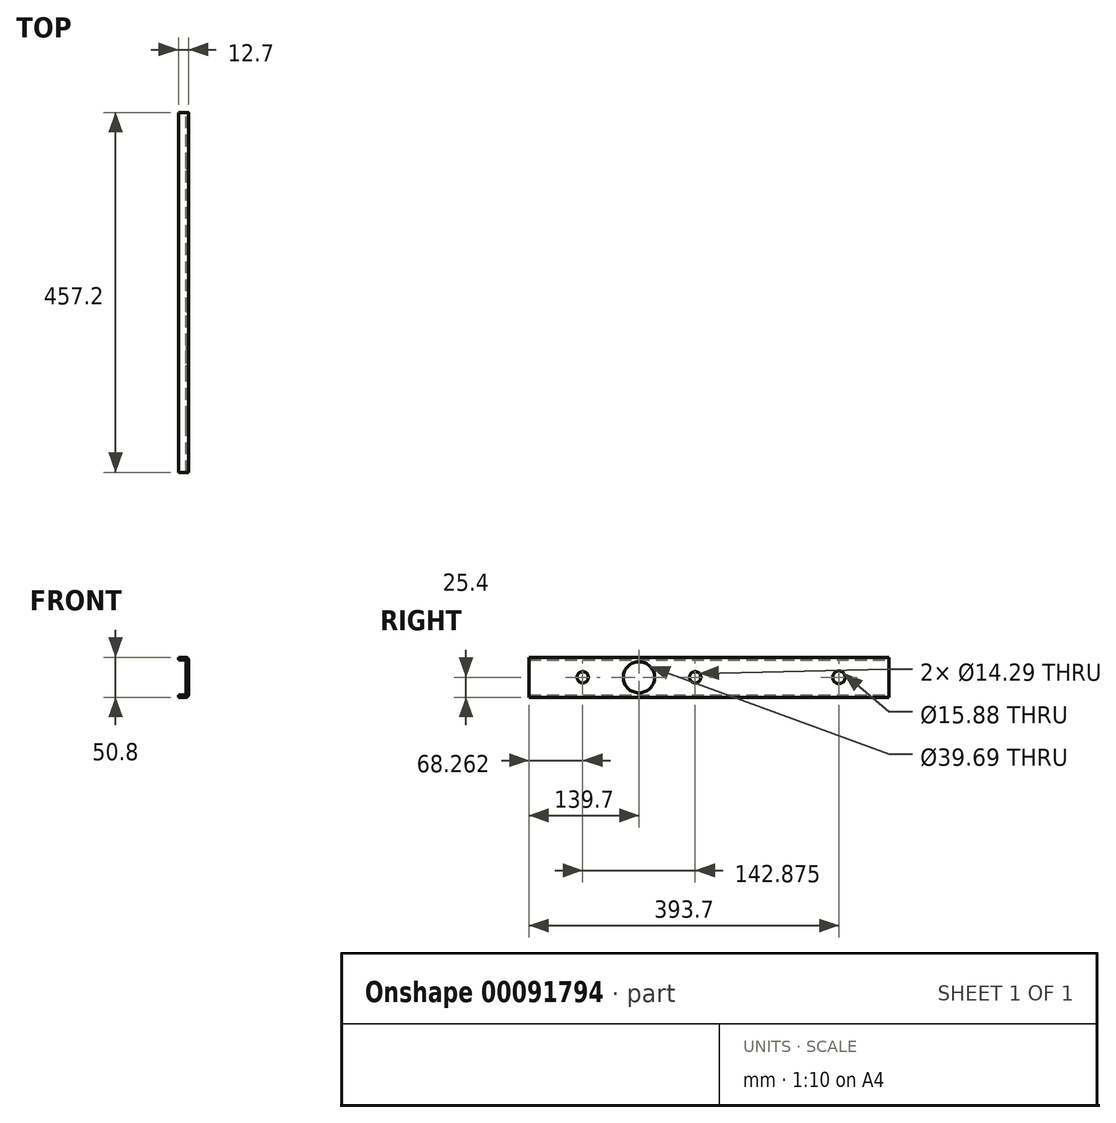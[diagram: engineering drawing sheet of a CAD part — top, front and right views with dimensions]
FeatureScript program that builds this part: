
annotation { "Feature Type Name" : "Feature", "Feature Type Description" : "" }
export const myFeature = defineFeature(function(context is Context, id is Id, definition is map)
    precondition{}
    {
        {
            var Q0;
            Q0=qCreatedBy(makeId("Front.planeOp"),FACE);
            var sketch = newSketch(context, id + "F0", { "sketchPlane" : qUnion([Q0])});
            skLineSegment(sketch, "E0", {"start": v(0, 0) * mm, "end": v(12.7, 0) * mm});
            skLineSegment(sketch, "E1", {"start": v(12.7, 0) * mm, "end": v(12.7, 50.8) * mm});
            skLineSegment(sketch, "E2", {"start": v(12.7, 50.8) * mm, "end": v(0, 50.8) * mm});
            skLineSegment(sketch, "E3", {"start": v(0, 50.8) * mm, "end": v(0, 47.63) * mm});
            skLineSegment(sketch, "E4", {"start": v(0, 47.63) * mm, "end": v(9.53, 47.63) * mm});
            skLineSegment(sketch, "E5", {"start": v(9.53, 47.63) * mm, "end": v(9.53, 3.18) * mm});
            skLineSegment(sketch, "E6", {"start": v(9.53, 3.18) * mm, "end": v(0, 3.18) * mm});
            skLineSegment(sketch, "E7", {"start": v(0, 3.18) * mm, "end": v(0, 0) * mm});
            skSolve(sketch);
        }
        {
            var Q0;
            Q0 = qSketchRegion(id + "F0", true);
            extrude(context, id + "F1", {"entities" : qUnion([Q0]), "depth" : 457.2 * mm});
        }
        {
            var Q0;
            Q0=makeQuery(id+"F1.opExtrude","SWEPT_EDGE",EDGE,{"disambiguationData":[OSD([sQuery(id+"F0.wireOp",EDGE,"E5"),sQuery(id+"F0.wireOp",EDGE,"E6")])]});
            var Q1;
            Q1=makeQuery(id+"F1.opExtrude","SWEPT_EDGE",EDGE,{"disambiguationData":[OSD([sQuery(id+"F0.wireOp",EDGE,"E4"),sQuery(id+"F0.wireOp",EDGE,"E5")])]});
            fillet(context, id + "F2", {"entities" : qUnion([Q0, Q1]), "radius" : 1.59 * mm, "tangentPropagation" : true, "allowEdgeOverflow" : false});
        }
        {
            var Q0;
            Q0=makeQuery(id+"F1.opExtrude","SWEPT_EDGE",EDGE,{"disambiguationData":[OSD([sQuery(id+"F0.wireOp",EDGE,"E0"),sQuery(id+"F0.wireOp",EDGE,"E1")])]});
            var Q1;
            Q1=makeQuery(id+"F1.opExtrude","SWEPT_EDGE",EDGE,{"disambiguationData":[OSD([sQuery(id+"F0.wireOp",EDGE,"E1"),sQuery(id+"F0.wireOp",EDGE,"E2")])]});
            fillet(context, id + "F3", {"entities" : qUnion([Q0, Q1]), "radius" : 3.17 * mm, "tangentPropagation" : true, "allowEdgeOverflow" : false});
        }
        {
            var Q0;
            Q0=makeQuery(id+"F1.opExtrude","SWEPT_FACE",FACE,{"disambiguationData":[OSD([sQuery(id+"F0.wireOp",EDGE,"E1")])]});
            var sketch = newSketch(context, id + "F4", { "sketchPlane" : qUnion([Q0])});
            skCircle(sketch, "E8", {"center": v(-388.94, 25.4) * mm, "radius": 7.14 * mm});
            skPoint(sketch, "E8.centerSnap0", {"position": v(-457.2, 25.4) * mm});
            skCircle(sketch, "E9", {"center": v(-246.06, 25.4) * mm, "radius": 7.14 * mm});
            skCircle(sketch, "E10", {"center": v(-317.5, 25.4) * mm, "radius": 19.84 * mm});
            skCircle(sketch, "E11", {"center": v(-63.5, 25.4) * mm, "radius": 7.94 * mm});
            skPoint(sketch, "E11.centerSnap0", {"position": v(0, 25.4) * mm});
            skSolve(sketch);
        }
        {
            var Q0;
            Q0 = qSketchRegion(id + "F4", true);
            extrude(context, id + "F5", {"entities" : qUnion([Q0]), "operationType" : NewBodyOperationType.REMOVE, "oppositeDirection" : true, "depth" : 25.4 * mm});
        }
    });
